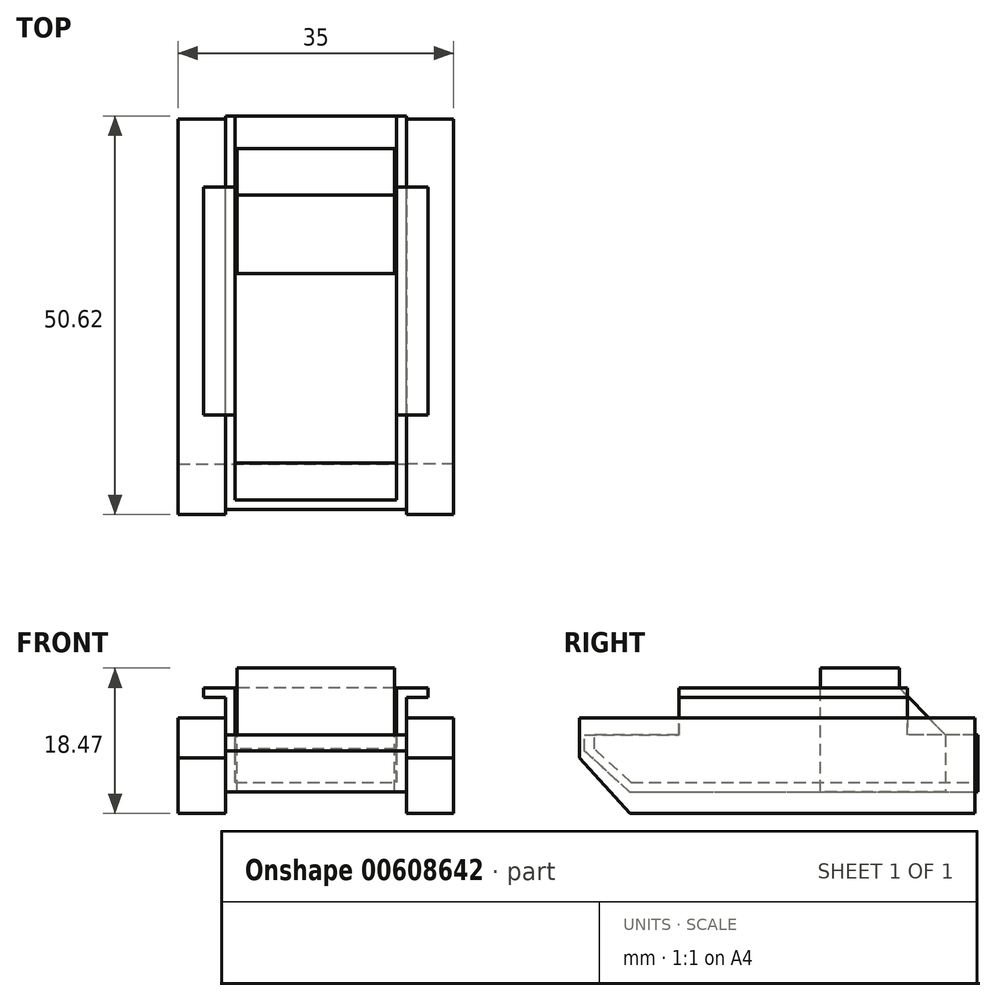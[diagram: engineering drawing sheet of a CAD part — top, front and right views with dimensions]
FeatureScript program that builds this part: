
annotation { "Feature Type Name" : "Feature", "Feature Type Description" : "" }
export const myFeature = defineFeature(function(context is Context, id is Id, definition is map)
    precondition{}
    {
        {
            var Q0;
            Q0=qCreatedBy(makeId("Front.planeOp"),FACE);
            var sketch = newSketch(context, id + "F0", { "sketchPlane" : qUnion([Q0])});
            skLineSegment(sketch, "E0.top", {"start": v(10.25, -6) * mm, "end": v(-10.25, -6) * mm});
            skLineSegment(sketch, "E0.left", {"start": v(10.25, 6) * mm, "end": v(10.25, -6) * mm});
            skLineSegment(sketch, "E0.right", {"start": v(-10.25, 6) * mm, "end": v(-10.25, -6) * mm});
            skPoint(sketch, "E0.middle", {"position": v(0, 0) * mm});
            skLineSegment(sketch, "E1", {"start": v(10.25, 6) * mm, "end": v(14.25, 6) * mm});
            skLineSegment(sketch, "E2", {"start": v(14.25, 6) * mm, "end": v(14.25, 4.75) * mm});
            skLineSegment(sketch, "E3", {"start": v(14.25, 4.75) * mm, "end": v(11.5, 4.75) * mm});
            skLineSegment(sketch, "E4", {"start": v(11.5, 4.75) * mm, "end": v(11.5, -7.25) * mm});
            skLineSegment(sketch, "E5", {"start": v(11.5, -7.25) * mm, "end": v(-11.5, -7.25) * mm});
            skLineSegment(sketch, "E6", {"start": v(-11.5, -7.25) * mm, "end": v(-11.5, 4.75) * mm});
            skLineSegment(sketch, "E7", {"start": v(-11.5, 4.75) * mm, "end": v(-14.25, 4.75) * mm});
            skLineSegment(sketch, "E8", {"start": v(-14.25, 4.75) * mm, "end": v(-14.25, 6) * mm});
            skLineSegment(sketch, "E9", {"start": v(-14.25, 6) * mm, "end": v(-10.25, 6) * mm});
            skSolve(sketch);
        }
        {
            var Q0;
            Q0=makeQuery(id+"F0.imprint","IMPRINT",FACE,{"disambiguationData":[TD([[makeQuery(id+"F0.imprint","IMPRINT",EDGE,{"derivedFrom":sQuery(id+"F0.wireOp",EDGE,"E0.top")}),1.0]])]});
            extrude(context, id + "F1", {"entities" : qUnion([Q0]), "depth" : 50 * mm, "offsetDistance" : 25 * mm});
        }
        {
            var Q0;
            Q0=qCreatedBy(makeId("Right.planeOp"),FACE);
            var sketch = newSketch(context, id + "F2", { "sketchPlane" : qUnion([Q0])});
            skLineSegment(sketch, "E10", {"start": v(0, 0) * mm, "end": v(-9, 0) * mm});
            skLineSegment(sketch, "E11", {"start": v(-9, 0) * mm, "end": v(-9, 8.9) * mm});
            skLineSegment(sketch, "E12", {"start": v(-9, 8.9) * mm, "end": v(-38, 8.9) * mm});
            skLineSegment(sketch, "E13", {"start": v(-38, 8.9) * mm, "end": v(-38, 0) * mm});
            skLineSegment(sketch, "E14", {"start": v(-38, 0) * mm, "end": v(-50, 0) * mm});
            skLineSegment(sketch, "E15", {"start": v(-50, 0) * mm, "end": v(-50, -2) * mm});
            skLineSegment(sketch, "E16", {"start": v(-50, -2) * mm, "end": v(-43.47, -8) * mm});
            skLineSegment(sketch, "E17", {"start": v(-43.47, -8) * mm, "end": v(-52.4, -8) * mm});
            skLineSegment(sketch, "E18", {"start": v(-52.4, -8) * mm, "end": v(-52.4, 11.73) * mm});
            skLineSegment(sketch, "E19", {"start": v(-52.4, 11.73) * mm, "end": v(2.34, 11.73) * mm});
            skLineSegment(sketch, "E20", {"start": v(2.34, 11.73) * mm, "end": v(2.34, 0) * mm});
            skLineSegment(sketch, "E21", {"start": v(2.34, 0) * mm, "end": v(0, 0) * mm});
            skSolve(sketch);
        }
        {
            var Q0;
            Q0=makeQuery(id+"F2.imprint","IMPRINT",FACE,{"disambiguationData":[TD([[makeQuery(id+"F2.imprint","IMPRINT",EDGE,{"derivedFrom":sQuery(id+"F2.wireOp",EDGE,"E10")}),-1.0]])]});
            extrude(context, id + "F3", {"entities" : qUnion([Q0]), "operationType" : NewBodyOperationType.REMOVE, "endBound" : BoundingType.SYMMETRIC, "oppositeDirection" : true, "depth" : 50 * mm, "offsetDistance" : 25 * mm});
        }
        {
            var Q0;
            Q0=qCreatedBy(makeId("Right.planeOp"),FACE);
            var sketch = newSketch(context, id + "F4", { "sketchPlane" : qUnion([Q0])});
            skLineSegment(sketch, "E22", {"start": v(-50, 0) * mm, "end": v(-48.75, 0) * mm});
            skLineSegment(sketch, "E23", {"start": v(-48.75, 0) * mm, "end": v(-48.75, -1.77) * mm});
            skLineSegment(sketch, "E24", {"start": v(-48.75, -1.77) * mm, "end": v(-42.7, -7.25) * mm});
            skLineSegment(sketch, "E25", {"start": v(-42.7, -7.25) * mm, "end": v(-44.28, -7.25) * mm});
            skLineSegment(sketch, "E26", {"start": v(-44.28, -7.25) * mm, "end": v(-50, -2) * mm});
            skLineSegment(sketch, "E27", {"start": v(-50, -2) * mm, "end": v(-50, 0) * mm});
            skSolve(sketch);
        }
        {
            var Q0;
            Q0=makeQuery(id+"F4.imprint","IMPRINT",FACE,{"disambiguationData":[TD([[makeQuery(id+"F4.imprint","IMPRINT",EDGE,{"derivedFrom":sQuery(id+"F4.wireOp",EDGE,"E22")}),-1.0]])]});
            extrude(context, id + "F5", {"entities" : qUnion([Q0]), "operationType" : NewBodyOperationType.ADD, "endBound" : BoundingType.SYMMETRIC, "depth" : 23 * mm, "offsetDistance" : 25 * mm});
        }
        {
            var Q0;
            Q0=qCreatedBy(makeId("Right.planeOp"),FACE);
            var sketch = newSketch(context, id + "F6", { "sketchPlane" : qUnion([Q0])});
            skLineSegment(sketch, "E28", {"start": v(-20.01, 6) * mm, "end": v(-20.01, 8.5) * mm});
            skLineSegment(sketch, "E29", {"start": v(-20.01, 8.5) * mm, "end": v(-10.01, 8.5) * mm});
            skLineSegment(sketch, "E30", {"start": v(-10.01, 8.5) * mm, "end": v(-10.01, 5.99) * mm});
            skLineSegment(sketch, "E31", {"start": v(-10.01, 5.99) * mm, "end": v(-4.15, 0) * mm});
            skLineSegment(sketch, "E32", {"start": v(-4.15, 0) * mm, "end": v(-4.15, -7.2) * mm});
            skLineSegment(sketch, "E33", {"start": v(-4.15, -7.2) * mm, "end": v(-20.01, -7.2) * mm});
            skLineSegment(sketch, "E34", {"start": v(-20.01, -7.2) * mm, "end": v(-20.01, 6) * mm});
            skLineSegment(sketch, "E35", {"start": v(-20.01, -7.2) * mm, "end": v(-20.01, -7.2) * mm});
            skSolve(sketch);
        }
        {
            var Q0;
            Q0=makeQuery(id+"F6.imprint","IMPRINT",FACE,{"disambiguationData":[TD([[makeQuery(id+"F6.imprint","IMPRINT",EDGE,{"derivedFrom":sQuery(id+"F6.wireOp",EDGE,"E28")}),-1.0]])]});
            var Q1;
            Q1=sQuery(id+"F6.wireOp",EDGE,"E33");
            var Q2;
            Q2=sQuery(id+"F6.wireOp",EDGE,"E32");
            var Q3;
            Q3=sQuery(id+"F6.wireOp",EDGE,"E29");
            var Q4;
            Q4=sQuery(id+"F6.wireOp",EDGE,"E28");
            var Q5;
            Q5=sQuery(id+"F6.wireOp",EDGE,"E31");
            var Q6;
            Q6=sQuery(id+"F6.wireOp",EDGE,"E34");
            var Q7;
            Q7=sQuery(id+"F6.wireOp",EDGE,"E30");
            extrude(context, id + "F7", {"entities" : qUnion([Q0]), "surfaceEntities" : qUnion([Q1, Q2, Q3, Q4, Q5, Q6, Q7]), "endBound" : BoundingType.SYMMETRIC, "depth" : 20 * mm, "offsetDistance" : 25 * mm});
        }
        {
            var Q0;
            Q0=makeQuery(id+"F1.opExtrude","SWEPT_FACE",FACE,{"disambiguationData":[OSD([sQuery(id+"F0.wireOp",EDGE,"E4")])]});
            var sketch = newSketch(context, id + "F8", { "sketchPlane" : qUnion([Q0])});
            skLineSegment(sketch, "E36", {"start": v(-38, 4.67) * mm, "end": v(-38, 2.17) * mm});
            skLineSegment(sketch, "E37", {"start": v(-38, 2.17) * mm, "end": v(-50.62, 2.17) * mm});
            skLineSegment(sketch, "E38", {"start": v(-50.62, 2.17) * mm, "end": v(-50.62, -2.92) * mm});
            skLineSegment(sketch, "E39", {"start": v(-50.62, -2.92) * mm, "end": v(-44.2, -9.96) * mm});
            skLineSegment(sketch, "E40", {"start": v(-44.2, -9.96) * mm, "end": v(-0.41, -9.96) * mm});
            skLineSegment(sketch, "E41", {"start": v(-0.41, -9.96) * mm, "end": v(-0.41, 2.17) * mm});
            skLineSegment(sketch, "E42", {"start": v(-0.41, 2.17) * mm, "end": v(-38, 2.17) * mm});
            skSolve(sketch);
        }
        {
            var Q0;
            Q0 = qSketchRegion(id + "F8", true);
            extrude(context, id + "F9", {"entities" : qUnion([Q0]), "operationType" : NewBodyOperationType.ADD, "depth" : 6 * mm, "offsetDistance" : 25 * mm});
        }
        {
            var Q0;
            Q0=makeQuery(id+"F1.opExtrude","SWEPT_BODY",BODY,{"disambiguationData":[OSD([sQuery(id+"F0.wireOp",EDGE,"E0.top"),sQuery(id+"F0.wireOp",EDGE,"E0.left"),sQuery(id+"F0.wireOp",EDGE,"E0.right"),sQuery(id+"F0.wireOp",EDGE,"E1"),sQuery(id+"F0.wireOp",EDGE,"E2"),sQuery(id+"F0.wireOp",EDGE,"E3"),sQuery(id+"F0.wireOp",EDGE,"E4"),sQuery(id+"F0.wireOp",EDGE,"E5"),sQuery(id+"F0.wireOp",EDGE,"E6"),sQuery(id+"F0.wireOp",EDGE,"E7"),sQuery(id+"F0.wireOp",EDGE,"E8"),sQuery(id+"F0.wireOp",EDGE,"E9")])]});
            var Q1;
            Q1=qCreatedBy(makeId("Right.planeOp"),FACE);
            mirror(context, id + "F10", {"entities" : qUnion([Q0]), "mirrorPlane" : qUnion([Q1])});
        }
    });
